# Revit family: ENCBMTYP007
name_source: partatom
category: Furniture
units: mm (PartAtom-declared; Revit-internal decimal feet)

## family parameters
Always vertical = Yes
Cut with Voids When Loaded = No
OmniClass Number = 23.40.20.00
OmniClass Title = General Furniture and Specialties
Render Appearance Source = Family Geometry
Room Calculation Point = No
Shared = No
Work Plane-Based = No

## types (1)
- ENCBMTYP007
    Cost = 75940 $
    Default Elevation = 0 mm  [stored 0 ft]
    Description = 6 x Frameless Glass Upmount Kit 12h X 54w, 2 x 51" ELECTRICAL JUMPER  (PT 30E), 3 x Universal Spine Glass Insert Screen - .375 12H x 72W, 3 x Encounter PwrBeam Double Sided Powered Spine Kit 72, 2 x Encounter PwrBeam Raceway Endcap Painted, 2 x Encounter PwrBeam 18 inch T-Leg for 29h, 2 x Encounter PwrBeam Vertical Support (for Storage Top Mnt), 6 x TBL, REC, 2mm, 24Dx60Wx29H, HAL, GLD, 2 x Cbx Credenza Shared With Sliding Door Lh 18dx21hx48w, 1 x Cbx Credenza Shared With Sliding Door Rh 18dx21hx48w, 6 x Cbx Suspended Hat Modesty 12h For 60w (44 Actual), 3 x CBX Side Access Roll Out Tower LH 24Dx42Hx15W, 3 x CBX Side Access Roll Out Tower RH 24Dx42Hx15W
    Exported From CET Designer = Yes
    Manufacturer = AIS
    Model = A-FGUM1254
    Show ENCBMTYP007 = Yes
    VisibilityIndex = 0

note: [stored X ft] marks values corroborated as IEEE doubles in the binary element streams (Revit-internal decimal feet)

## geometry (parser evidence)
native form markers: Sweep x3
no freeform markers — native parametric forms only
